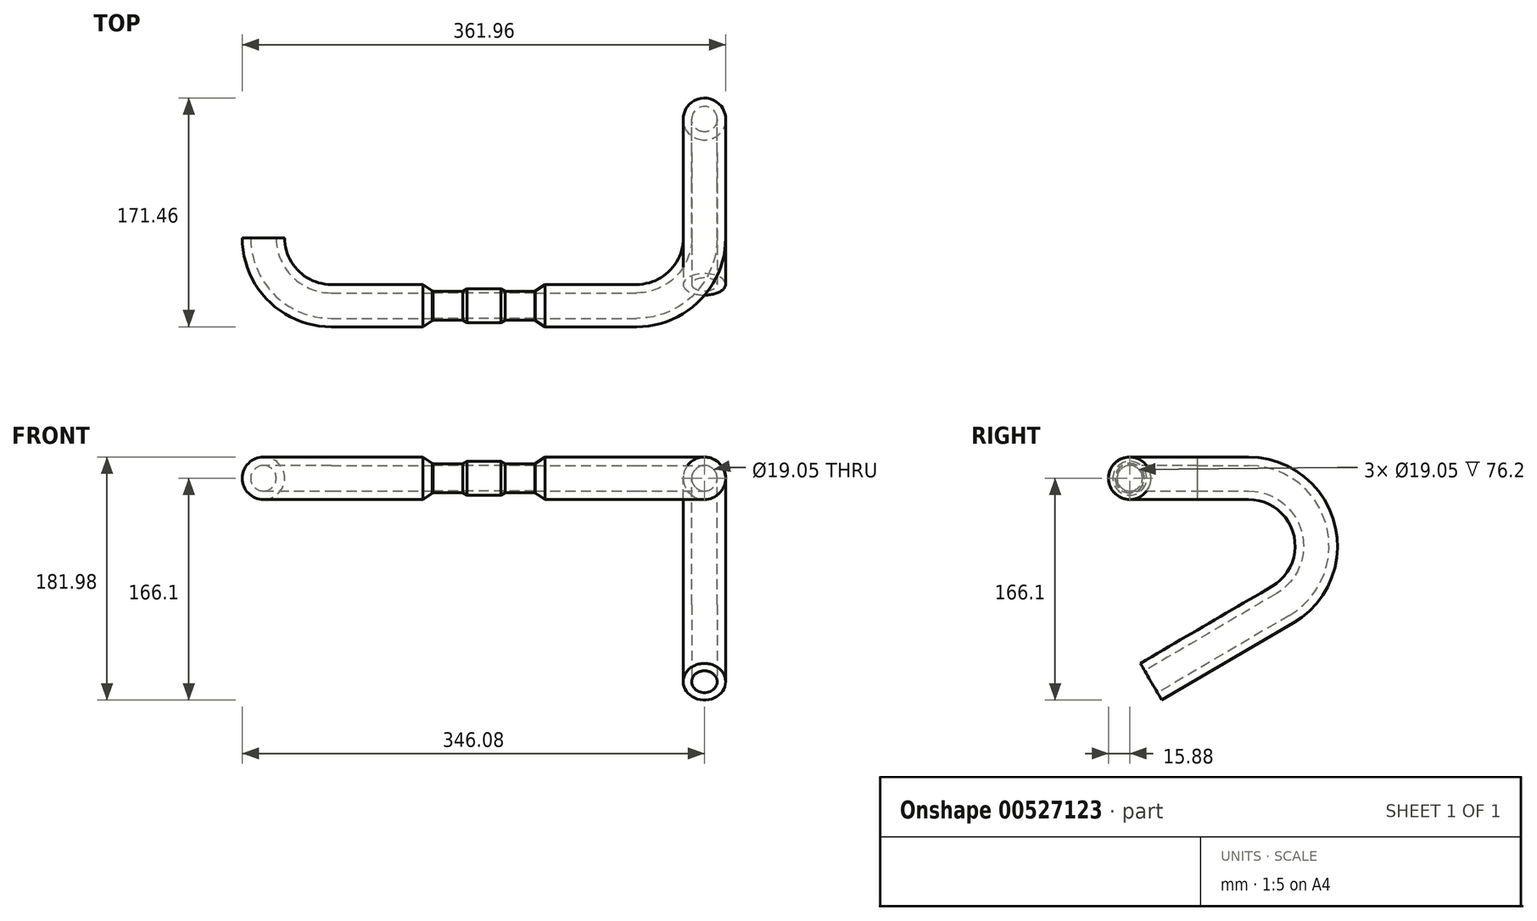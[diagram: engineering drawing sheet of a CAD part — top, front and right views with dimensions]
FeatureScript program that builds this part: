
annotation { "Feature Type Name" : "Feature", "Feature Type Description" : "" }
export const myFeature = defineFeature(function(context is Context, id is Id, definition is map)
    precondition{}
    {
        {
            var Q0;
            Q0=qCreatedBy(makeId("Top.planeOp"),FACE);
            var sketch = newSketch(context, id + "F0", { "sketchPlane" : qUnion([Q0])});
            skLineSegment(sketch, "E0.bottom", {"start": v(114.3, 0) * mm, "end": v(165.1, 0) * mm});
            skLineSegment(sketch, "E0.top", {"start": v(114.3, 50.8) * mm, "end": v(165.1, 50.8) * mm});
            skLineSegment(sketch, "E0.left", {"start": v(114.3, 0) * mm, "end": v(114.3, 50.8) * mm});
            skLineSegment(sketch, "E0.right", {"start": v(165.1, 0) * mm, "end": v(165.1, 50.8) * mm});
            skArc(sketch, "E1", {"start": v(114.3, 0) * mm, "mid": v(150.22, 14.88) * mm, "end": v(165.1, 50.8) * mm});
            skLineSegment(sketch, "E2", {"start": v(0, 0) * mm, "end": v(38.1, 0) * mm});
            skLineSegment(sketch, "E3", {"start": v(38.1, 0) * mm, "end": v(114.3, 0) * mm});
            skLineSegment(sketch, "E4", {"start": v(0, 0) * mm, "end": v(12.7, 0) * mm});
            skSolve(sketch);
        }
        {
            var Q0;
            Q0=qCreatedBy(makeId("Right.planeOp"),FACE);
            var sketch = newSketch(context, id + "F1", { "sketchPlane" : qUnion([Q0])});
            skCircle(sketch, "E5", {"center": v(0, 0) * mm, "radius": 11.11 * mm});
            skCircle(sketch, "E6.0", {"center": v(0, 0) * mm, "radius": 9.53 * mm});
            skCircle(sketch, "E7", {"center": v(0, 0) * mm, "radius": 15.88 * mm});
            skSolve(sketch);
        }
        {
            var Q0;
            Q0=qCreatedBy(makeId("Right.planeOp"),FACE);
            var sketch = newSketch(context, id + "F2", { "sketchPlane" : qUnion([Q0])});
            skLineSegment(sketch, "E8", {"start": v(0, 0) * mm, "end": v(38.1, 0) * mm});
            skArc(sketch, "E9", {"start": v(38.1, 0) * mm, "mid": v(87.13, -37.5) * mm, "end": v(63.77, -94.64) * mm});
            skLineSegment(sketch, "E10", {"start": v(63.77, -94.64) * mm, "end": v(-34.86, -152.4) * mm});
            skLineSegment(sketch, "E11", {"start": v(-34.86, 0) * mm, "end": v(-34.86, -152.4) * mm});
            skSolve(sketch);
        }
        {
            var Q0;
            Q0=makeQuery(id+"F1.imprint","IMPRINT",FACE,{"disambiguationData":[TD([[makeQuery(id+"F1.imprint","IMPRINT",EDGE,{"derivedFrom":sQuery(id+"F1.wireOp",EDGE,"E5")}),1.0]])]});
            var Q1;
            Q1=sQuery(id+"F0.wireOp",EDGE,"E2");
            sweep(context, id + "F3", {"profiles" : qUnion([Q0]), "path" : qUnion([Q1])});
        }
        {
            var Q0;
            Q0=makeQuery(id+"F3.opSweep","CAP_FACE",FACE,{"disambiguationData":[OSD([sQuery(id+"F0.wireOp",VERTEX,"E2.end"),sQuery(id+"F1.wireOp",EDGE,"E5"),sQuery(id+"F1.wireOp",EDGE,"E6.0")])],"isStart":false});
            var sketch = newSketch(context, id + "F4", { "sketchPlane" : qUnion([Q0])});
            skCircle(sketch, "E12", {"center": v(0, 0) * mm, "radius": 11.11 * mm});
            skCircle(sketch, "E13", {"center": v(0, 0) * mm, "radius": 9.53 * mm});
            skCircle(sketch, "E14", {"center": v(0, 0) * mm, "radius": 15.88 * mm});
            skSolve(sketch);
        }
        {
            var Q0;
            Q0=makeQuery(id+"F4.imprint","IMPRINT",FACE,{"disambiguationData":[TD([[makeQuery(id+"F4.imprint","IMPRINT",EDGE,{"derivedFrom":sQuery(id+"F4.wireOp",EDGE,"E12")}),-1.0]])]});
            var Q1;
            Q1=makeQuery(id+"F4.imprint","IMPRINT",FACE,{"disambiguationData":[TD([[makeQuery(id+"F4.imprint","IMPRINT",EDGE,{"derivedFrom":sQuery(id+"F4.wireOp",EDGE,"E12")}),1.0]])]});
            var Q2;
            Q2=sQuery(id+"F0.wireOp",EDGE,"E3");
            var Q3;
            Q3=sQuery(id+"F0.wireOp",EDGE,"E1");
            sweep(context, id + "F5", {"operationType" : NewBodyOperationType.ADD, "profiles" : qUnion([Q0, Q1]), "path" : qUnion([Q2, Q3])});
        }
        {
            var Q0;
            Q0=qCreatedBy(makeId("Front.planeOp"),FACE);
            var sketch = newSketch(context, id + "F6", { "sketchPlane" : qUnion([Q0])});
            skCircle(sketch, "E15", {"center": v(0, 0) * mm, "radius": 11.11 * mm});
            skCircle(sketch, "E16", {"center": v(0, 0) * mm, "radius": 9.53 * mm});
            skCircle(sketch, "E17", {"center": v(0, 0) * mm, "radius": 15.88 * mm});
            skSolve(sketch);
        }
        {
            var Q0;
            Q0=makeQuery(id+"F6.imprint","IMPRINT",FACE,{"disambiguationData":[TD([[makeQuery(id+"F6.imprint","IMPRINT",EDGE,{"derivedFrom":sQuery(id+"F6.wireOp",EDGE,"E15")}),-1.0]])]});
            var Q1;
            Q1=makeQuery(id+"F6.imprint","IMPRINT",FACE,{"disambiguationData":[TD([[makeQuery(id+"F6.imprint","IMPRINT",EDGE,{"derivedFrom":sQuery(id+"F6.wireOp",EDGE,"E15")}),1.0]])]});
            var Q2;
            Q2=sQuery(id+"F2.wireOp",EDGE,"E8");
            var Q3;
            Q3=sQuery(id+"F2.wireOp",EDGE,"E9");
            var Q4;
            Q4=sQuery(id+"F2.wireOp",EDGE,"E10");
            sweep(context, id + "F7", {"profiles" : qUnion([Q0, Q1]), "path" : qUnion([Q2, Q3, Q4])});
        }
        {
            var Q0;
            Q0=makeQuery(id+"F7.opSweep","SWEPT_BODY",BODY,{"disambiguationData":[OSD([sQuery(id+"F2.wireOp",EDGE,"E10"),sQuery(id+"F6.wireOp",EDGE,"E16"),sQuery(id+"F6.wireOp",EDGE,"E17")])]});
            transform(context, id + "F8", {"entities" : qUnion([Q0]), "transformType" : TransformType.TRANSLATION_3D, "dx" : 165.1 * mm, "dy" : 50.8 * mm, "dz" : 0 * mm, "makeCopy" : false});
        }
        {
            var Q0;
            Q0=makeQuery(id+"F5.opSweep","CAP_EDGE",EDGE,{"disambiguationData":[OSD([sQuery(id+"F0.wireOp",VERTEX,"E3.start"),sQuery(id+"F4.wireOp",EDGE,"E14")])],"isStart":true});
            chamfer(context, id + "F9", {"entities" : qUnion([Q0]), "chamferType" : ChamferType.TWO_OFFSETS, "width1" : 7.62 * mm, "oppositeDirection" : false, "width2" : 5.08 * mm, "tangentPropagation" : true});
        }
        {
            var Q0;
            Q0=makeQuery(id+"F3.opSweep","SWEPT_BODY",BODY,{"disambiguationData":[OSD([sQuery(id+"F0.wireOp",EDGE,"E2"),sQuery(id+"F1.wireOp",EDGE,"E5"),sQuery(id+"F1.wireOp",EDGE,"E6.0")])]});
            var Q1;
            Q1=qCreatedBy(makeId("Right.planeOp"),FACE);
            mirror(context, id + "F10", {"operationType" : NewBodyOperationType.ADD, "entities" : qUnion([Q0]), "mirrorPlane" : qUnion([Q1])});
        }
        {
            var Q0;
            Q0=qCreatedBy(makeId("Front.planeOp"),FACE);
            var sketch = newSketch(context, id + "F11", { "sketchPlane" : qUnion([Q0])});
            skLineSegment(sketch, "E18.bottom", {"start": v(38.1, 25.4) * mm, "end": v(-38.1, 25.4) * mm});
            skLineSegment(sketch, "E18.top", {"start": v(38.1, -25.4) * mm, "end": v(-38.1, -25.4) * mm});
            skLineSegment(sketch, "E18.left", {"start": v(38.1, 25.4) * mm, "end": v(38.1, -25.4) * mm});
            skLineSegment(sketch, "E18.right", {"start": v(-38.1, 25.4) * mm, "end": v(-38.1, -25.4) * mm});
            skPoint(sketch, "E18.middle", {"position": v(0, 0) * mm});
            skSolve(sketch);
        }
        {
            var Q0;
            Q0 = qSketchRegion(id + "F11", true);
            extrude(context, id + "F12", {"entities" : qUnion([Q0]), "operationType" : NewBodyOperationType.REMOVE, "depth" : 76.2 * mm, "offsetDistance" : 25.4 * mm, "symmetric" : true});
        }
        {
            var Q0;
            Q0=qCreatedBy(makeId("Front.planeOp"),FACE);
            var sketch = newSketch(context, id + "F13", { "sketchPlane" : qUnion([Q0])});
            skLineSegment(sketch, "E19.bottom", {"start": v(-38.1, 10.8) * mm, "end": v(38.1, 10.8) * mm});
            skLineSegment(sketch, "E19.top", {"start": v(-38.1, -10.8) * mm, "end": v(38.1, -10.8) * mm});
            skLineSegment(sketch, "E19.left", {"start": v(-38.1, 10.8) * mm, "end": v(-38.1, -10.8) * mm});
            skLineSegment(sketch, "E19.right", {"start": v(38.1, 10.8) * mm, "end": v(38.1, -10.8) * mm});
            skPoint(sketch, "E19.middle", {"position": v(0, 0) * mm});
            skLineSegment(sketch, "E20.bottom", {"start": v(-38.1, 9.53) * mm, "end": v(38.1, 9.53) * mm});
            skLineSegment(sketch, "E20.top", {"start": v(-38.1, -9.53) * mm, "end": v(38.1, -9.53) * mm});
            skLineSegment(sketch, "E20.left", {"start": v(-38.1, 9.53) * mm, "end": v(-38.1, -9.53) * mm});
            skLineSegment(sketch, "E20.right", {"start": v(38.1, 9.53) * mm, "end": v(38.1, -9.53) * mm});
            skLineSegment(sketch, "E21.bottom", {"start": v(-12.7, 12.7) * mm, "end": v(12.7, 12.7) * mm});
            skLineSegment(sketch, "E21.top", {"start": v(-12.7, -12.7) * mm, "end": v(12.7, -12.7) * mm});
            skLineSegment(sketch, "E21.left", {"start": v(-12.7, 12.7) * mm, "end": v(-12.7, -12.7) * mm});
            skLineSegment(sketch, "E21.right", {"start": v(12.7, 12.7) * mm, "end": v(12.7, -12.7) * mm});
            skLineSegment(sketch, "E22", {"start": v(-12.7, 12.7) * mm, "end": v(-16, 10.8) * mm});
            skLineSegment(sketch, "E23", {"start": v(12.7, 12.7) * mm, "end": v(16, 10.8) * mm});
            skSolve(sketch);
        }
        {
            var Q0;
            {var subQ5=sQuery(id+"F13.wireOp",EDGE,"E19.bottom");var subQ7=makeQuery(id+"F13.imprint","INTERSECT",VERTEX,{"derivedFrom":[subQ5,sQuery(id+"F13.wireOp",EDGE,"E23")]});Q0=makeQuery(id+"F13.imprint","IMPRINT",FACE,{"disambiguationData":[TD([[makeQuery(id+"F13.imprint","IMPRINT",EDGE,{"disambiguationData":[TD([[subQ7,-1.0]])],"derivedFrom":subQ5}),-1.0]])]});}
            var Q1;
            {var subQ0=sQuery(id+"F13.wireOp",EDGE,"E21.left");var subQ1=sQuery(id+"F13.wireOp",EDGE,"E19.bottom");var subQ2=makeQuery(id+"F13.imprint","INTERSECT",VERTEX,{"derivedFrom":[subQ1,subQ0]});Q1=makeQuery(id+"F13.imprint","IMPRINT",FACE,{"disambiguationData":[TD([[makeQuery(id+"F13.imprint","IMPRINT",EDGE,{"disambiguationData":[TD([[subQ2,-1.0]])],"derivedFrom":subQ1}),-1.0]])]});}
            var Q2;
            {var subQ5=sQuery(id+"F13.wireOp",EDGE,"E21.bottom");Q2=makeQuery(id+"F13.imprint","IMPRINT",FACE,{"disambiguationData":[TD([[makeQuery(id+"F13.imprint","IMPRINT",EDGE,{"derivedFrom":subQ5}),-1.0]])]});}
            var Q3;
            {var subQ0=sQuery(id+"F13.wireOp",EDGE,"E23");Q3=makeQuery(id+"F13.imprint","IMPRINT",FACE,{"disambiguationData":[TD([[makeQuery(id+"F13.imprint","IMPRINT",EDGE,{"derivedFrom":subQ0}),-1.0]])]});}
            var Q4;
            {var subQ5=sQuery(id+"F13.wireOp",EDGE,"E19.bottom");var subQ8=makeQuery(id+"F13.imprint","INTERSECT",VERTEX,{"derivedFrom":[subQ5,sQuery(id+"F13.wireOp",EDGE,"E22")]});Q4=makeQuery(id+"F13.imprint","IMPRINT",FACE,{"disambiguationData":[TD([[makeQuery(id+"F13.imprint","IMPRINT",EDGE,{"disambiguationData":[TD([[subQ8,1.0]])],"derivedFrom":subQ5}),-1.0]])]});}
            var Q5;
            {var subQ3=sQuery(id+"F13.wireOp",EDGE,"E22");Q5=makeQuery(id+"F13.imprint","IMPRINT",FACE,{"disambiguationData":[TD([[makeQuery(id+"F13.imprint","IMPRINT",EDGE,{"derivedFrom":subQ3}),1.0]])]});}
            var Q6;
            Q6=sQuery(id+"F0.wireOp",EDGE,"E2");
            revolve(context, id + "F14", {"entities" : qUnion([Q0, Q1, Q2, Q3, Q4, Q5]), "axis" : qUnion([Q6]), "revolveType" : RevolveType.FULL});
        }
    });
